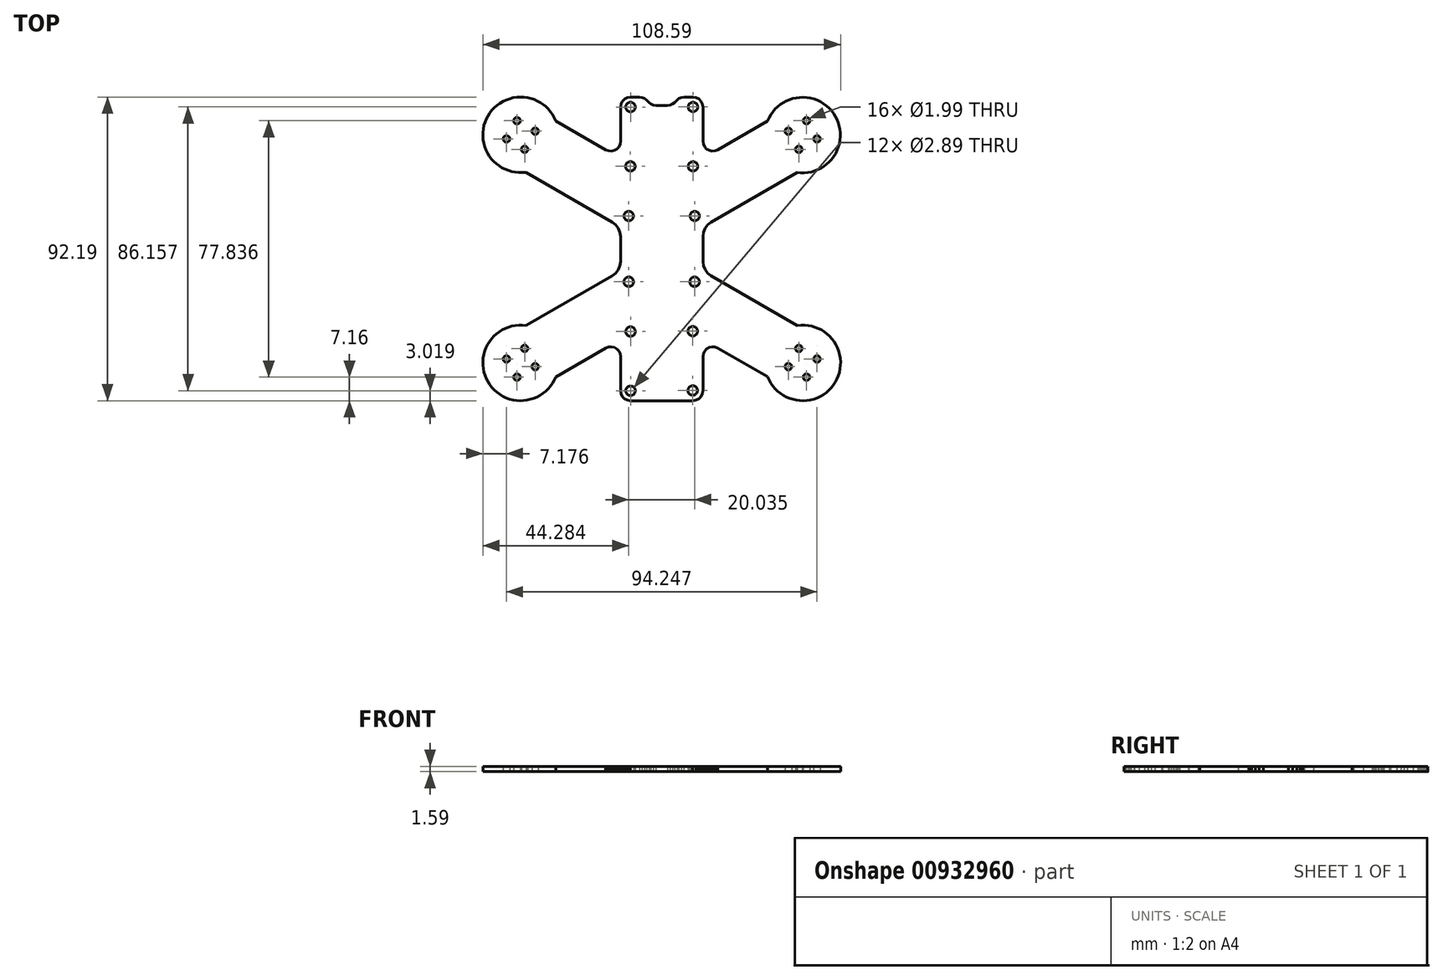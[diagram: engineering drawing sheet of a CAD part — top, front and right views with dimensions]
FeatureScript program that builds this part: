
annotation { "Feature Type Name" : "Feature", "Feature Type Description" : "" }
export const myFeature = defineFeature(function(context is Context, id is Id, definition is map)
    precondition{}
    {
        {
            var Q0;
            Q0=qCreatedBy(makeId("Top.planeOp"),FACE);
            var sketch = newSketch(context, id + "F0", { "sketchPlane" : qUnion([Q0])});
            skArc(sketch, "E0", {"start": v(-29.86, 35.61) * mm, "mid": v(-50.46, 37.2) * mm, "end": v(-38.94, 20.05) * mm});
            skArc(sketch, "E1", {"start": v(34.42, -42.05) * mm, "mid": v(55.02, -43.58) * mm, "end": v(43.46, -26.46) * mm});
            skArc(sketch, "E2", {"start": v(-38.88, -26.47) * mm, "mid": v(-50.49, -43.55) * mm, "end": v(-29.88, -42.08) * mm});
            skCircle(sketch, "E3", {"center": v(-7.74, -13.2) * mm, "radius": 1.44 * mm});
            skCircle(sketch, "E4", {"center": v(12.26, -13.2) * mm, "radius": 1.44 * mm});
            skCircle(sketch, "E5", {"center": v(-7.2, -28.3) * mm, "radius": 1.44 * mm});
            skCircle(sketch, "E6", {"center": v(11.69, -28.2) * mm, "radius": 1.44 * mm});
            skCircle(sketch, "E7", {"center": v(-7.2, -46.28) * mm, "radius": 1.44 * mm});
            skCircle(sketch, "E8", {"center": v(11.69, -46.2) * mm, "radius": 1.44 * mm});
            skCircle(sketch, "E9", {"center": v(-7.73, 6.77) * mm, "radius": 1.44 * mm});
            skCircle(sketch, "E10", {"center": v(12.3, 6.77) * mm, "radius": 1.44 * mm});
            skCircle(sketch, "E11", {"center": v(-7.23, 21.85) * mm, "radius": 1.44 * mm});
            skCircle(sketch, "E12", {"center": v(11.77, 21.85) * mm, "radius": 1.44 * mm});
            skCircle(sketch, "E13", {"center": v(11.77, 39.88) * mm, "radius": 1.44 * mm});
            skCircle(sketch, "E14", {"center": v(-7.2, 39.86) * mm, "radius": 1.44 * mm});
            skCircle(sketch, "E15", {"center": v(40.7, 32.52) * mm, "radius": 1 * mm});
            skCircle(sketch, "E16", {"center": v(49.4, 30.18) * mm, "radius": 1 * mm});
            skCircle(sketch, "E17", {"center": v(46.23, 35.7) * mm, "radius": 1 * mm});
            skCircle(sketch, "E18", {"center": v(43.89, 27) * mm, "radius": 1 * mm});
            skCircle(sketch, "E19", {"center": v(46.23, -42.14) * mm, "radius": 1 * mm});
            skCircle(sketch, "E20", {"center": v(49.4, -36.64) * mm, "radius": 1 * mm});
            skCircle(sketch, "E21", {"center": v(43.89, -33.44) * mm, "radius": 1 * mm});
            skCircle(sketch, "E22", {"center": v(40.7, -38.96) * mm, "radius": 1 * mm});
            skCircle(sketch, "E23", {"center": v(-36.15, -38.96) * mm, "radius": 1 * mm});
            skCircle(sketch, "E24", {"center": v(-41.66, -42.14) * mm, "radius": 1 * mm});
            skCircle(sketch, "E25", {"center": v(-44.84, -36.64) * mm, "radius": 1 * mm});
            skCircle(sketch, "E26", {"center": v(-39.33, -33.44) * mm, "radius": 1 * mm});
            skCircle(sketch, "E27", {"center": v(-39.33, 27) * mm, "radius": 1 * mm});
            skCircle(sketch, "E28", {"center": v(-36.15, 32.52) * mm, "radius": 1 * mm});
            skCircle(sketch, "E29", {"center": v(-44.84, 30.18) * mm, "radius": 1 * mm});
            skCircle(sketch, "E30", {"center": v(-41.66, 35.7) * mm, "radius": 1 * mm});
            skLineSegment(sketch, "E31", {"start": v(-38.88, -26.47) * mm, "end": v(-38.8, -26.42) * mm});
            skLineSegment(sketch, "E32", {"start": v(-38.8, -26.42) * mm, "end": v(-12.74, -11.38) * mm});
            skLineSegment(sketch, "E33", {"start": v(-12.74, -11.38) * mm, "end": v(-11.7, -10.57) * mm});
            skLineSegment(sketch, "E34", {"start": v(-11.7, -10.57) * mm, "end": v(-10.9, -9.54) * mm});
            skLineSegment(sketch, "E35", {"start": v(-10.9, -9.54) * mm, "end": v(-10.4, -8.34) * mm});
            skLineSegment(sketch, "E36", {"start": v(-10.4, -8.34) * mm, "end": v(-10.22, -7.04) * mm});
            skLineSegment(sketch, "E37", {"start": v(-10.22, -7.04) * mm, "end": v(-10.22, 0.6) * mm});
            skLineSegment(sketch, "E38", {"start": v(-10.22, 0.6) * mm, "end": v(-10.4, 1.89) * mm});
            skLineSegment(sketch, "E39", {"start": v(-10.4, 1.89) * mm, "end": v(-10.9, 3.1) * mm});
            skLineSegment(sketch, "E40", {"start": v(-10.9, 3.1) * mm, "end": v(-11.69, 4.13) * mm});
            skLineSegment(sketch, "E41", {"start": v(-11.69, 4.13) * mm, "end": v(-12.72, 4.92) * mm});
            skLineSegment(sketch, "E42", {"start": v(-12.72, 4.92) * mm, "end": v(-38.94, 20.05) * mm});
            skLineSegment(sketch, "E43", {"start": v(-29.88, -42.08) * mm, "end": v(-14.72, -33.3) * mm});
            skLineSegment(sketch, "E44", {"start": v(-14.72, -33.3) * mm, "end": v(-13.89, -32.98) * mm});
            skLineSegment(sketch, "E45", {"start": v(-13.89, -32.98) * mm, "end": v(-13, -32.91) * mm});
            skLineSegment(sketch, "E46", {"start": v(-13, -32.91) * mm, "end": v(-12.13, -33.11) * mm});
            skLineSegment(sketch, "E47", {"start": v(-12.13, -33.11) * mm, "end": v(-11.35, -33.56) * mm});
            skLineSegment(sketch, "E48", {"start": v(-11.35, -33.56) * mm, "end": v(-10.75, -34.21) * mm});
            skLineSegment(sketch, "E49", {"start": v(-10.75, -34.21) * mm, "end": v(-10.36, -35.02) * mm});
            skLineSegment(sketch, "E50", {"start": v(-10.36, -35.02) * mm, "end": v(-10.22, -35.9) * mm});
            skLineSegment(sketch, "E51", {"start": v(-10.22, -35.9) * mm, "end": v(-10.22, -46.3) * mm});
            skLineSegment(sketch, "E52", {"start": v(-10.22, -46.3) * mm, "end": v(-10.07, -47.23) * mm});
            skLineSegment(sketch, "E53", {"start": v(-10.07, -47.23) * mm, "end": v(-9.66, -48.05) * mm});
            skLineSegment(sketch, "E54", {"start": v(-9.66, -48.05) * mm, "end": v(-9, -48.72) * mm});
            skLineSegment(sketch, "E55", {"start": v(-9, -48.72) * mm, "end": v(-8.14, -49.15) * mm});
            skLineSegment(sketch, "E56", {"start": v(-8.14, -49.15) * mm, "end": v(-7.22, -49.3) * mm});
            skLineSegment(sketch, "E57", {"start": v(-7.22, -49.3) * mm, "end": v(11.69, -49.3) * mm});
            skLineSegment(sketch, "E58", {"start": v(11.69, -49.3) * mm, "end": v(12.64, -49.15) * mm});
            skLineSegment(sketch, "E59", {"start": v(12.64, -49.15) * mm, "end": v(13.5, -48.7) * mm});
            skLineSegment(sketch, "E60", {"start": v(13.5, -48.7) * mm, "end": v(14.19, -48.02) * mm});
            skLineSegment(sketch, "E61", {"start": v(14.19, -48.02) * mm, "end": v(14.63, -47.16) * mm});
            skLineSegment(sketch, "E62", {"start": v(14.63, -47.16) * mm, "end": v(14.78, -46.2) * mm});
            skLineSegment(sketch, "E63", {"start": v(14.78, -46.2) * mm, "end": v(14.78, -35.9) * mm});
            skLineSegment(sketch, "E64", {"start": v(14.78, -35.9) * mm, "end": v(14.91, -35.02) * mm});
            skLineSegment(sketch, "E65", {"start": v(14.91, -35.02) * mm, "end": v(15.3, -34.22) * mm});
            skLineSegment(sketch, "E66", {"start": v(15.3, -34.22) * mm, "end": v(15.9, -33.56) * mm});
            skLineSegment(sketch, "E67", {"start": v(15.9, -33.56) * mm, "end": v(16.68, -33.11) * mm});
            skLineSegment(sketch, "E68", {"start": v(16.68, -33.11) * mm, "end": v(17.55, -32.91) * mm});
            skLineSegment(sketch, "E69", {"start": v(17.55, -32.91) * mm, "end": v(18.45, -32.98) * mm});
            skLineSegment(sketch, "E70", {"start": v(18.45, -32.98) * mm, "end": v(19.28, -33.3) * mm});
            skLineSegment(sketch, "E71", {"start": v(19.28, -33.3) * mm, "end": v(34.42, -42.05) * mm});
            skLineSegment(sketch, "E72", {"start": v(43.46, -26.46) * mm, "end": v(17.28, -11.37) * mm});
            skLineSegment(sketch, "E73", {"start": v(17.28, -11.37) * mm, "end": v(16.24, -10.57) * mm});
            skLineSegment(sketch, "E74", {"start": v(16.24, -10.57) * mm, "end": v(15.45, -9.54) * mm});
            skLineSegment(sketch, "E75", {"start": v(15.45, -9.54) * mm, "end": v(14.95, -8.33) * mm});
            skLineSegment(sketch, "E76", {"start": v(14.95, -8.33) * mm, "end": v(14.78, -7.04) * mm});
            skLineSegment(sketch, "E77", {"start": v(14.78, -7.04) * mm, "end": v(14.78, 0.6) * mm});
            skLineSegment(sketch, "E78", {"start": v(14.78, 0.6) * mm, "end": v(14.95, 1.89) * mm});
            skLineSegment(sketch, "E79", {"start": v(14.95, 1.89) * mm, "end": v(15.45, 3.1) * mm});
            skLineSegment(sketch, "E80", {"start": v(15.45, 3.1) * mm, "end": v(16.24, 4.13) * mm});
            skLineSegment(sketch, "E81", {"start": v(16.24, 4.13) * mm, "end": v(17.28, 4.92) * mm});
            skLineSegment(sketch, "E82", {"start": v(19.28, 26.87) * mm, "end": v(18.45, 26.54) * mm});
            skLineSegment(sketch, "E83", {"start": v(18.45, 26.54) * mm, "end": v(17.54, 26.47) * mm});
            skLineSegment(sketch, "E84", {"start": v(17.54, 26.47) * mm, "end": v(16.68, 26.67) * mm});
            skLineSegment(sketch, "E85", {"start": v(16.68, 26.67) * mm, "end": v(15.9, 27.12) * mm});
            skLineSegment(sketch, "E86", {"start": v(15.9, 27.12) * mm, "end": v(15.3, 27.77) * mm});
            skLineSegment(sketch, "E87", {"start": v(15.3, 27.77) * mm, "end": v(14.91, 28.58) * mm});
            skLineSegment(sketch, "E88", {"start": v(14.91, 28.58) * mm, "end": v(14.78, 29.45) * mm});
            skLineSegment(sketch, "E89", {"start": v(14.78, 29.45) * mm, "end": v(14.78, 39.84) * mm});
            skLineSegment(sketch, "E90", {"start": v(14.78, 39.84) * mm, "end": v(14.64, 40.77) * mm});
            skLineSegment(sketch, "E91", {"start": v(14.64, 40.77) * mm, "end": v(14.2, 41.61) * mm});
            skLineSegment(sketch, "E92", {"start": v(14.2, 41.61) * mm, "end": v(13.54, 42.29) * mm});
            skLineSegment(sketch, "E93", {"start": v(13.54, 42.29) * mm, "end": v(12.7, 42.7) * mm});
            skLineSegment(sketch, "E94", {"start": v(12.7, 42.7) * mm, "end": v(11.78, 42.85) * mm});
            skLineSegment(sketch, "E95", {"start": v(11.78, 42.85) * mm, "end": v(9.03, 42.85) * mm});
            skLineSegment(sketch, "E96", {"start": v(9.03, 42.85) * mm, "end": v(8.25, 42.75) * mm});
            skLineSegment(sketch, "E97", {"start": v(8.25, 42.75) * mm, "end": v(7.52, 42.45) * mm});
            skLineSegment(sketch, "E98", {"start": v(7.52, 42.45) * mm, "end": v(6.9, 41.98) * mm});
            skLineSegment(sketch, "E99", {"start": v(6.9, 41.98) * mm, "end": v(6.16, 41.24) * mm});
            skLineSegment(sketch, "E100", {"start": v(6.16, 41.24) * mm, "end": v(5.54, 40.76) * mm});
            skLineSegment(sketch, "E101", {"start": v(5.54, 40.76) * mm, "end": v(4.81, 40.46) * mm});
            skLineSegment(sketch, "E102", {"start": v(4.81, 40.46) * mm, "end": v(4.06, 40.36) * mm});
            skLineSegment(sketch, "E103", {"start": v(4.06, 40.36) * mm, "end": v(0.52, 40.36) * mm});
            skLineSegment(sketch, "E104", {"start": v(0.52, 40.36) * mm, "end": v(-0.25, 40.45) * mm});
            skLineSegment(sketch, "E105", {"start": v(-0.25, 40.45) * mm, "end": v(-0.99, 40.76) * mm});
            skLineSegment(sketch, "E106", {"start": v(-0.99, 40.76) * mm, "end": v(-1.6, 41.23) * mm});
            skLineSegment(sketch, "E107", {"start": v(-1.6, 41.23) * mm, "end": v(-2.33, 41.97) * mm});
            skLineSegment(sketch, "E108", {"start": v(-2.33, 41.97) * mm, "end": v(-2.96, 42.45) * mm});
            skLineSegment(sketch, "E109", {"start": v(-2.96, 42.45) * mm, "end": v(-3.69, 42.75) * mm});
            skLineSegment(sketch, "E110", {"start": v(-3.69, 42.75) * mm, "end": v(-4.47, 42.85) * mm});
            skLineSegment(sketch, "E111", {"start": v(-4.47, 42.85) * mm, "end": v(-7.22, 42.85) * mm});
            skLineSegment(sketch, "E112", {"start": v(-7.22, 42.85) * mm, "end": v(-8.14, 42.7) * mm});
            skLineSegment(sketch, "E113", {"start": v(-8.14, 42.7) * mm, "end": v(-8.98, 42.28) * mm});
            skLineSegment(sketch, "E114", {"start": v(-8.98, 42.28) * mm, "end": v(-9.65, 41.62) * mm});
            skLineSegment(sketch, "E115", {"start": v(-9.65, 41.62) * mm, "end": v(-10.08, 40.78) * mm});
            skLineSegment(sketch, "E116", {"start": v(-10.08, 40.78) * mm, "end": v(-10.22, 39.85) * mm});
            skLineSegment(sketch, "E117", {"start": v(-10.22, 39.85) * mm, "end": v(-10.22, 29.47) * mm});
            skLineSegment(sketch, "E118", {"start": v(-10.22, 29.47) * mm, "end": v(-10.36, 28.6) * mm});
            skLineSegment(sketch, "E119", {"start": v(-10.36, 28.6) * mm, "end": v(-10.74, 27.77) * mm});
            skLineSegment(sketch, "E120", {"start": v(-10.74, 27.77) * mm, "end": v(-11.35, 27.12) * mm});
            skLineSegment(sketch, "E121", {"start": v(-11.35, 27.12) * mm, "end": v(-12.12, 26.67) * mm});
            skLineSegment(sketch, "E122", {"start": v(-12.12, 26.67) * mm, "end": v(-12.99, 26.48) * mm});
            skLineSegment(sketch, "E123", {"start": v(-12.99, 26.48) * mm, "end": v(-13.89, 26.54) * mm});
            skLineSegment(sketch, "E124", {"start": v(-13.89, 26.54) * mm, "end": v(-14.72, 26.87) * mm});
            skLineSegment(sketch, "E125", {"start": v(-14.72, 26.87) * mm, "end": v(-29.86, 35.61) * mm});
            skLineSegment(sketch, "E126", {"start": v(17.28, 4.92) * mm, "end": v(43.35, 19.98) * mm});
            skArc(sketch, "E127", {"start": v(43.35, 19.98) * mm, "mid": v(54.98, 37.05) * mm, "end": v(34.38, 35.6) * mm});
            skLineSegment(sketch, "E128", {"start": v(19.28, 26.87) * mm, "end": v(34.38, 35.6) * mm});
            skSolve(sketch);
        }
        {
            var Q0;
            Q0=makeQuery(id+"F0.imprint","IMPRINT",FACE,{"disambiguationData":[TD([[makeQuery(id+"F0.imprint","IMPRINT",EDGE,{"derivedFrom":sQuery(id+"F0.wireOp",EDGE,"E0")}),1.0]])]});
            extrude(context, id + "F1", {"entities" : qUnion([Q0]), "depth" : 1.59 * mm, "offsetDistance" : 25.4 * mm});
        }
    });
